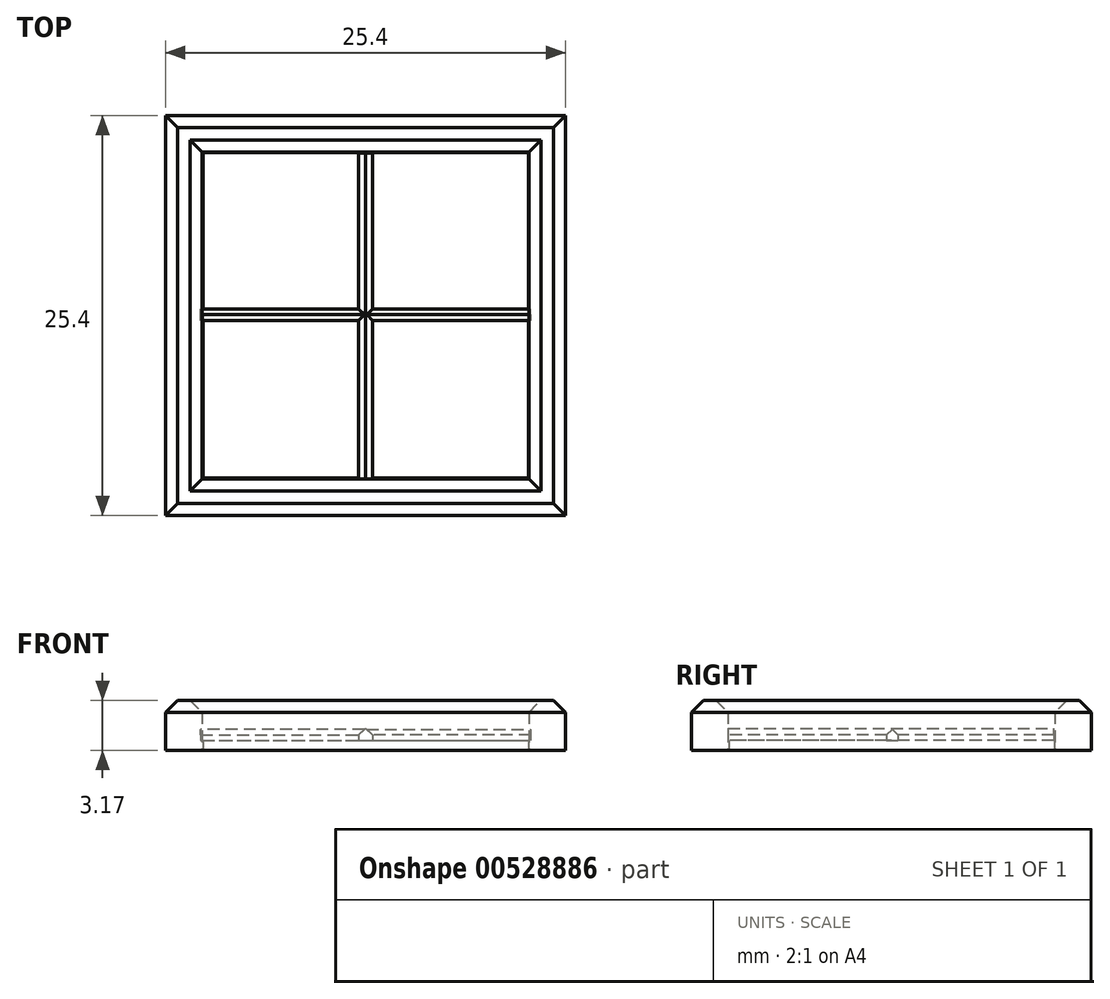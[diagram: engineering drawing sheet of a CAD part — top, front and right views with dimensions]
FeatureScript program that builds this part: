
annotation { "Feature Type Name" : "Feature", "Feature Type Description" : "" }
export const myFeature = defineFeature(function(context is Context, id is Id, definition is map)
    precondition{}
    {
        {
            var Q0;
            Q0=qCreatedBy(makeId("Top.planeOp"),FACE);
            var sketch = newSketch(context, id + "F0", { "sketchPlane" : qUnion([Q0])});
            skLineSegment(sketch, "E0.bottom", {"start": v(-40.03, -42.59) * mm, "end": v(-14.63, -42.59) * mm});
            skLineSegment(sketch, "E0.top", {"start": v(-40.03, -17.19) * mm, "end": v(-14.63, -17.19) * mm});
            skLineSegment(sketch, "E0.left", {"start": v(-40.03, -42.59) * mm, "end": v(-40.03, -17.19) * mm});
            skLineSegment(sketch, "E0.right", {"start": v(-14.63, -42.59) * mm, "end": v(-14.63, -17.19) * mm});
            skLineSegment(sketch, "E1", {"start": v(-37.7, -19.51) * mm, "end": v(-37.7, -40.26) * mm});
            skLineSegment(sketch, "E2", {"start": v(-16.96, -40.26) * mm, "end": v(-37.7, -40.26) * mm});
            skLineSegment(sketch, "E3", {"start": v(-37.7, -19.51) * mm, "end": v(-16.96, -19.51) * mm});
            skLineSegment(sketch, "E4", {"start": v(-16.96, -40.26) * mm, "end": v(-16.96, -19.51) * mm});
            skSolve(sketch);
        }
        {
            var Q0;
            Q0 = qSketchRegion(id + "F0", true);
            extrude(context, id + "F1", {"entities" : qUnion([Q0]), "depth" : 3.17 * mm, "offsetDistance" : 25.4 * mm});
        }
        {
            var Q0;
            Q0=qCreatedBy(makeId("Top.planeOp"),FACE);
            var sketch = newSketch(context, id + "F2", { "sketchPlane" : qUnion([Q0])});
            skLineSegment(sketch, "E5.bottom", {"start": v(-37.66, -19.54) * mm, "end": v(-16.99, -19.54) * mm});
            skLineSegment(sketch, "E5.top", {"start": v(-37.66, -40.22) * mm, "end": v(-16.99, -40.22) * mm});
            skLineSegment(sketch, "E5.left", {"start": v(-37.66, -19.54) * mm, "end": v(-37.66, -40.22) * mm});
            skLineSegment(sketch, "E5.right", {"start": v(-16.99, -19.54) * mm, "end": v(-16.99, -40.22) * mm});
            skSolve(sketch);
        }
        {
            var Q0;
            Q0 = qSketchRegion(id + "F2", true);
            extrude(context, id + "F3", {"entities" : qUnion([Q0]), "depth" : 0.64 * mm, "offsetDistance" : 25.4 * mm});
        }
        {
            var Q0;
            Q0=makeQuery(id+"F3.opExtrude","CAP_FACE",FACE,{"disambiguationData":[OSD([sQuery(id+"F2.wireOp",EDGE,"E5.bottom"),sQuery(id+"F2.wireOp",EDGE,"E5.top"),sQuery(id+"F2.wireOp",EDGE,"E5.left"),sQuery(id+"F2.wireOp",EDGE,"E5.right")])],"isStart":false});
            var sketch = newSketch(context, id + "F4", { "sketchPlane" : qUnion([Q0])});
            skLineSegment(sketch, "E6", {"start": v(-16.99, -29.88) * mm, "end": v(-37.66, -29.88) * mm});
            skLineSegment(sketch, "E7", {"start": v(-27.33, -19.54) * mm, "end": v(-27.33, -40.22) * mm});
            skSolve(sketch);
        }
        {
            var Q0;
            {var subQ0=sQuery(id+"F4.wireOp",EDGE,"E6");var subQ1=makeQuery(id+"F3.opExtrude","CAP_EDGE",EDGE,{"disambiguationData":[OSD([sQuery(id+"F2.wireOp",EDGE,"E5.left")])],"isStart":false});var subQ2=makeQuery(id+"F4.imprint","INTERSECT",VERTEX,{"derivedFrom":[subQ1,subQ0]});Q0=makeQuery(id+"F4.imprint","IMPRINT",FACE,{"disambiguationData":[TD([[makeQuery(id+"F4.imprint","IMPRINT",EDGE,{"disambiguationData":[TD([[subQ2,1.0]])],"derivedFrom":subQ0}),-1.0]])]});}
            var sketch = newSketch(context, id + "F5", { "sketchPlane" : qUnion([Q0])});
            skLineSegment(sketch, "E8.bottom", {"start": v(-27.77, -19.58) * mm, "end": v(-26.88, -19.58) * mm});
            skLineSegment(sketch, "E8.top", {"start": v(-27.77, -40.27) * mm, "end": v(-26.88, -40.27) * mm});
            skLineSegment(sketch, "E8.left", {"start": v(-27.77, -19.58) * mm, "end": v(-27.77, -40.27) * mm});
            skLineSegment(sketch, "E8.right", {"start": v(-26.88, -19.58) * mm, "end": v(-26.88, -40.27) * mm});
            skLineSegment(sketch, "E9.bottom", {"start": v(-37.8, -30.2) * mm, "end": v(-16.85, -30.2) * mm});
            skLineSegment(sketch, "E9.top", {"start": v(-37.8, -29.46) * mm, "end": v(-16.85, -29.46) * mm});
            skLineSegment(sketch, "E9.left", {"start": v(-37.8, -30.2) * mm, "end": v(-37.8, -29.46) * mm});
            skLineSegment(sketch, "E9.right", {"start": v(-16.85, -30.2) * mm, "end": v(-16.85, -29.46) * mm});
            skSolve(sketch);
        }
        {
            var Q0;
            Q0 = qSketchRegion(id + "F5", true);
            extrude(context, id + "F6", {"entities" : qUnion([Q0]), "depth" : 0.76 * mm, "offsetDistance" : 25.4 * mm});
        }
        {
            var Q0;
            {var subQ0=sQuery(id+"F5.wireOp",EDGE,"E9.bottom");Q0=makeQuery(id+"F6.opExtrude","CAP_EDGE",EDGE,{"disambiguationData":[OSD([subQ0]),TDD([makeQuery(id+"F5.imprint","IMPRINT",EDGE,{"disambiguationData":[TD([[makeQuery(id+"F5.imprint","INTERSECT",VERTEX,{"derivedFrom":[subQ0,sQuery(id+"F5.wireOp",EDGE,"E9.left")]}),-1.0]])],"derivedFrom":subQ0})])],"isStart":false});}
            var Q1;
            {var subQ0=sQuery(id+"F5.wireOp",EDGE,"E9.top");Q1=makeQuery(id+"F6.opExtrude","CAP_EDGE",EDGE,{"disambiguationData":[OSD([subQ0]),TDD([makeQuery(id+"F5.imprint","IMPRINT",EDGE,{"disambiguationData":[TD([[makeQuery(id+"F5.imprint","INTERSECT",VERTEX,{"derivedFrom":[subQ0,sQuery(id+"F5.wireOp",EDGE,"E9.left")]}),-1.0]])],"derivedFrom":subQ0}),makeQuery(id+"F5.imprint","IMPRINT",EDGE,{"disambiguationData":[TD([[makeQuery(id+"F5.imprint","INTERSECT",VERTEX,{"derivedFrom":[sQuery(id+"F5.wireOp",EDGE,"E8.left"),subQ0]}),1.0]])],"derivedFrom":subQ0})])],"isStart":false});}
            var Q2;
            {var subQ0=sQuery(id+"F5.wireOp",EDGE,"E8.left");Q2=makeQuery(id+"F6.opExtrude","CAP_EDGE",EDGE,{"disambiguationData":[OSD([subQ0]),TDD([makeQuery(id+"F5.imprint","IMPRINT",EDGE,{"disambiguationData":[TD([[makeQuery(id+"F5.imprint","INTERSECT",VERTEX,{"derivedFrom":[sQuery(id+"F5.wireOp",EDGE,"E8.bottom"),subQ0]}),-1.0]])],"derivedFrom":subQ0})])],"isStart":false});}
            var Q3;
            {var subQ0=sQuery(id+"F5.wireOp",EDGE,"E8.right");Q3=makeQuery(id+"F6.opExtrude","CAP_EDGE",EDGE,{"disambiguationData":[OSD([subQ0]),TDD([makeQuery(id+"F5.imprint","IMPRINT",EDGE,{"disambiguationData":[TD([[makeQuery(id+"F5.imprint","INTERSECT",VERTEX,{"derivedFrom":[sQuery(id+"F5.wireOp",EDGE,"E8.bottom"),subQ0]}),-1.0]])],"derivedFrom":subQ0})])],"isStart":false});}
            var Q4;
            {var subQ0=sQuery(id+"F5.wireOp",EDGE,"E9.top");Q4=makeQuery(id+"F6.opExtrude","CAP_EDGE",EDGE,{"disambiguationData":[OSD([subQ0]),TDD([makeQuery(id+"F5.imprint","IMPRINT",EDGE,{"disambiguationData":[TD([[makeQuery(id+"F5.imprint","INTERSECT",VERTEX,{"derivedFrom":[subQ0,sQuery(id+"F5.wireOp",EDGE,"E9.right")]}),1.0]])],"derivedFrom":subQ0})])],"isStart":false});}
            var Q5;
            {var subQ0=sQuery(id+"F5.wireOp",EDGE,"E9.bottom");Q5=makeQuery(id+"F6.opExtrude","CAP_EDGE",EDGE,{"disambiguationData":[OSD([subQ0]),TDD([makeQuery(id+"F5.imprint","IMPRINT",EDGE,{"disambiguationData":[TD([[makeQuery(id+"F5.imprint","INTERSECT",VERTEX,{"derivedFrom":[subQ0,sQuery(id+"F5.wireOp",EDGE,"E9.right")]}),1.0]])],"derivedFrom":subQ0})])],"isStart":false});}
            var Q6;
            {var subQ0=sQuery(id+"F5.wireOp",EDGE,"E8.right");Q6=makeQuery(id+"F6.opExtrude","CAP_EDGE",EDGE,{"disambiguationData":[OSD([subQ0]),TDD([makeQuery(id+"F5.imprint","IMPRINT",EDGE,{"disambiguationData":[TD([[makeQuery(id+"F5.imprint","INTERSECT",VERTEX,{"derivedFrom":[sQuery(id+"F5.wireOp",EDGE,"E8.top"),subQ0]}),1.0]])],"derivedFrom":subQ0})])],"isStart":false});}
            var Q7;
            {var subQ0=sQuery(id+"F5.wireOp",EDGE,"E8.left");Q7=makeQuery(id+"F6.opExtrude","CAP_EDGE",EDGE,{"disambiguationData":[OSD([subQ0]),TDD([makeQuery(id+"F5.imprint","IMPRINT",EDGE,{"disambiguationData":[TD([[makeQuery(id+"F5.imprint","INTERSECT",VERTEX,{"derivedFrom":[sQuery(id+"F5.wireOp",EDGE,"E8.top"),subQ0]}),1.0]])],"derivedFrom":subQ0})])],"isStart":false});}
            chamfer(context, id + "F7", {"entities" : qUnion([Q0, Q1, Q2, Q3, Q4, Q5, Q6, Q7]), "width" : 0.43 * mm, "tangentPropagation" : true});
        }
        {
            var Q0;
            Q0=makeQuery(id+"F1.opExtrude","CAP_EDGE",EDGE,{"disambiguationData":[OSD([sQuery(id+"F0.wireOp",EDGE,"E0.right")])],"isStart":false});
            var Q1;
            Q1=makeQuery(id+"F1.opExtrude","CAP_EDGE",EDGE,{"disambiguationData":[OSD([sQuery(id+"F0.wireOp",EDGE,"E0.bottom")])],"isStart":false});
            var Q2;
            Q2=makeQuery(id+"F1.opExtrude","CAP_EDGE",EDGE,{"disambiguationData":[OSD([sQuery(id+"F0.wireOp",EDGE,"E0.left")])],"isStart":false});
            var Q3;
            Q3=makeQuery(id+"F1.opExtrude","CAP_EDGE",EDGE,{"disambiguationData":[OSD([sQuery(id+"F0.wireOp",EDGE,"E0.top")])],"isStart":false});
            var Q4;
            Q4=makeQuery(id+"F1.opExtrude","CAP_EDGE",EDGE,{"disambiguationData":[OSD([sQuery(id+"F0.wireOp",EDGE,"E1")])],"isStart":false});
            var Q5;
            Q5=makeQuery(id+"F1.opExtrude","CAP_EDGE",EDGE,{"disambiguationData":[OSD([sQuery(id+"F0.wireOp",EDGE,"E3")])],"isStart":false});
            var Q6;
            Q6=makeQuery(id+"F1.opExtrude","CAP_EDGE",EDGE,{"disambiguationData":[OSD([sQuery(id+"F0.wireOp",EDGE,"E4")])],"isStart":false});
            var Q7;
            Q7=makeQuery(id+"F1.opExtrude","CAP_EDGE",EDGE,{"disambiguationData":[OSD([sQuery(id+"F0.wireOp",EDGE,"E2")])],"isStart":false});
            chamfer(context, id + "F8", {"entities" : qUnion([Q0, Q1, Q2, Q3, Q4, Q5, Q6, Q7]), "width" : 0.76 * mm, "tangentPropagation" : true});
        }
    });
